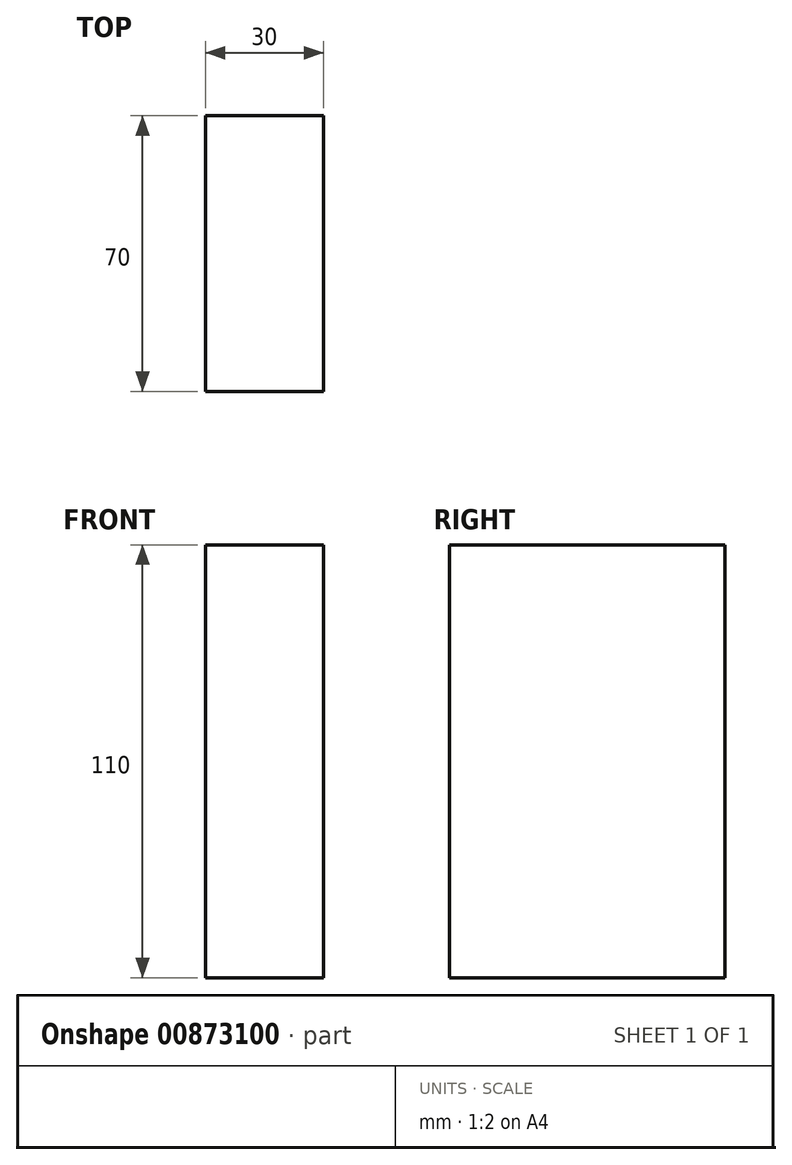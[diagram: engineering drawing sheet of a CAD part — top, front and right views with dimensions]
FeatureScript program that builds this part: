
annotation { "Feature Type Name" : "Feature", "Feature Type Description" : "" }
export const myFeature = defineFeature(function(context is Context, id is Id, definition is map)
    precondition{}
    {
        {
            var Q0;
            Q0=qCreatedBy(makeId("Right.planeOp"), FACE);
            var sketch = newSketch(context, id + "F0", { "sketchPlane" : qUnion([Q0])});
            skLineSegment(sketch, "E0.bottom", {"start": v(-35, 55) * mm, "end": v(35, 55) * mm});
            skLineSegment(sketch, "E0.top", {"start": v(-35, -55) * mm, "end": v(35, -55) * mm});
            skLineSegment(sketch, "E0.left", {"start": v(-35, 55) * mm, "end": v(-35, -55) * mm});
            skLineSegment(sketch, "E0.right", {"start": v(35, 55) * mm, "end": v(35, -55) * mm});
            skSolve(sketch);
        }
        {
            var Q0;
            Q0 = qSketchRegion(id + "F0", true);
            extrude(context, id + "F1", {"entities" : qUnion([Q0]), "endBound" : BoundingType.SYMMETRIC, "depth" : 30 * mm, "offsetDistance" : 25 * mm});
        }
    });
